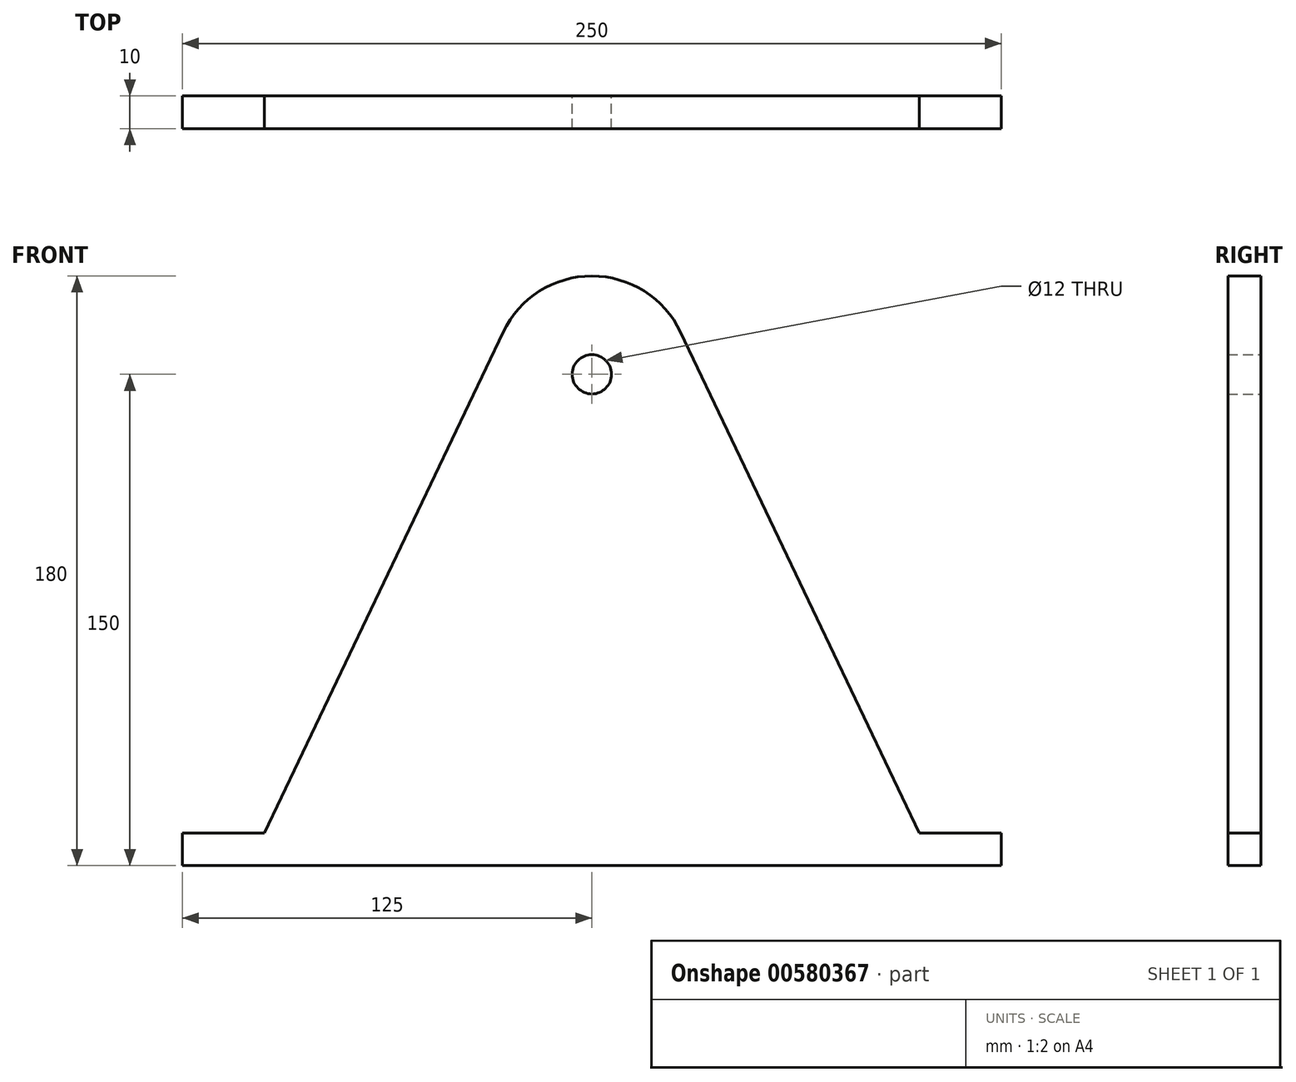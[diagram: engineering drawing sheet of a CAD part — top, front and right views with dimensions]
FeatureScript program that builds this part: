
annotation { "Feature Type Name" : "Feature", "Feature Type Description" : "" }
export const myFeature = defineFeature(function(context is Context, id is Id, definition is map)
    precondition{}
    {
        {
            var Q0;
            Q0=qCreatedBy(makeId("Front.planeOp"),FACE);
            var sketch = newSketch(context, id + "F0", { "sketchPlane" : qUnion([Q0])});
            skLineSegment(sketch, "E0", {"start": v(0, 0) * mm, "end": v(0, 140) * mm, "construction": true});
            skArc(sketch, "E1", {"start": v(27.08, 152.91) * mm, "mid": v(0, 170) * mm, "end": v(-27.08, 152.91) * mm});
            skLineSegment(sketch, "E2", {"start": v(-100, 0) * mm, "end": v(-27.08, 152.91) * mm});
            skLineSegment(sketch, "E3.MirrorCS", {"start": v(100, 0) * mm, "end": v(27.08, 152.91) * mm});
            skCircle(sketch, "E4", {"center": v(0, 140) * mm, "radius": 6 * mm});
            skPoint(sketch, "E5.middle", {"position": v(0, 0) * mm});
            skLineSegment(sketch, "E6.bottom", {"start": v(-125, 0) * mm, "end": v(-100, 0) * mm});
            skLineSegment(sketch, "E6.top", {"start": v(-125, -10) * mm, "end": v(125, -10) * mm});
            skLineSegment(sketch, "E6.left", {"start": v(-125, 0) * mm, "end": v(-125, -10) * mm});
            skLineSegment(sketch, "E6.right", {"start": v(125, 0) * mm, "end": v(125, -10) * mm});
            skLineSegment(sketch, "E7.trimOffspring", {"start": v(100, 0) * mm, "end": v(125, 0) * mm});
            skPoint(sketch, "E8.MirrorCS.end.orphan", {"position": v(100, 0) * mm});
            skSolve(sketch);
        }
        {
            var Q0;
            Q0=makeQuery(id+"F0.imprint","IMPRINT",FACE,{"disambiguationData":[TD([[makeQuery(id+"F0.imprint","IMPRINT",EDGE,{"derivedFrom":sQuery(id+"F0.wireOp",EDGE,"E1")}),1.0]])]});
            extrude(context, id + "F1", {"entities" : qUnion([Q0]), "depth" : 10 * mm, "offsetDistance" : 25 * mm});
        }
    });
